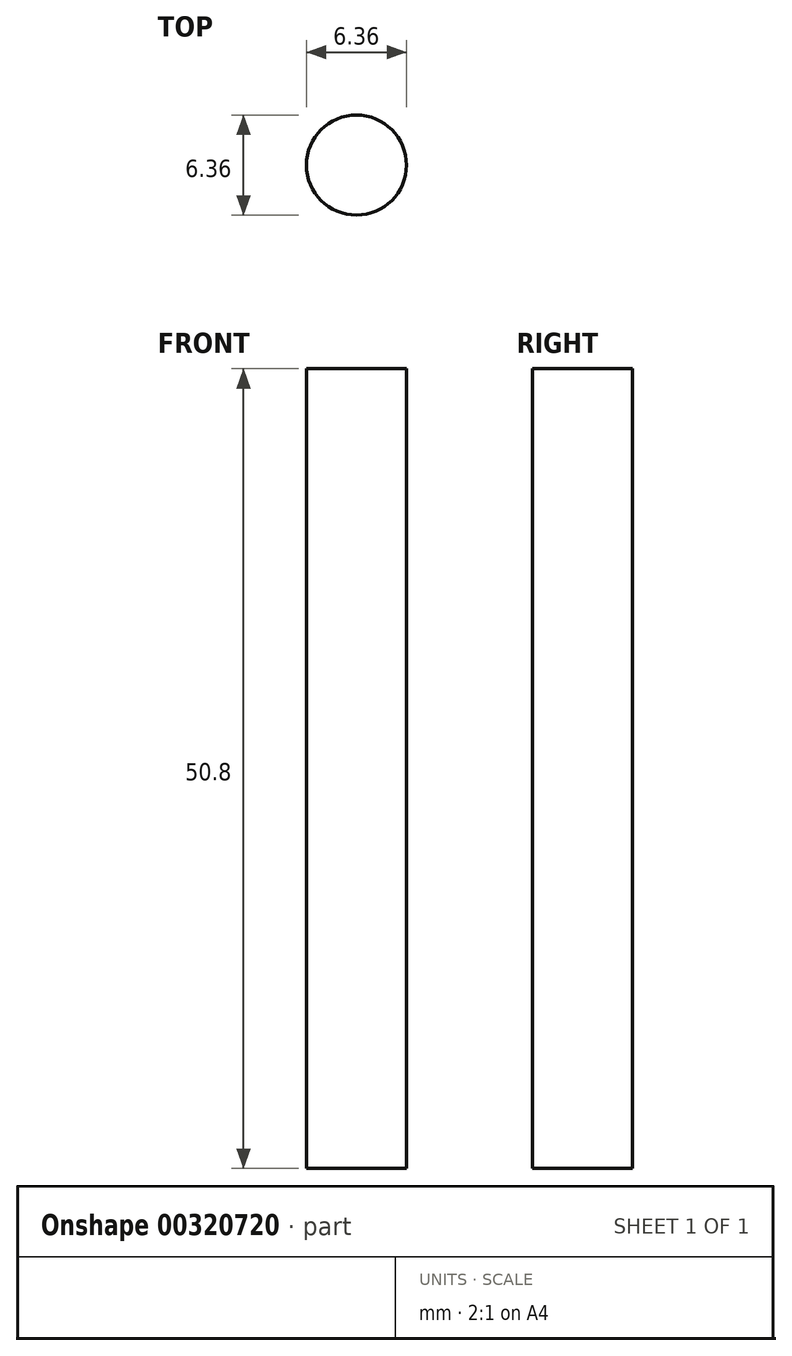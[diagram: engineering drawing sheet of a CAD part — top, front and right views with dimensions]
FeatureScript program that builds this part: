
annotation { "Feature Type Name" : "Feature", "Feature Type Description" : "" }
export const myFeature = defineFeature(function(context is Context, id is Id, definition is map)
    precondition{}
    {
        {
            var Q0;
            Q0=qCreatedBy(makeId("Top.planeOp"),FACE);
            var sketch = newSketch(context, id + "F0", { "sketchPlane" : qUnion([Q0])});
            skCircle(sketch, "E0", {"center": v(0, 0) * mm, "radius": 3.18 * mm});
            skSolve(sketch);
        }
        {
            var Q0;
            Q0=qSketchRegion(id+"F0",true);
            extrude(context, id + "F1", {"entities" : qUnion([Q0]), "depth" : 50.8 * mm});
        }
    });
